# Revit family: STARC-REALWALL-PANEL
name_source: partatom
category: Specialty Equipment
revit_build: Autodesk Revit 2014 (Build: 20140709_2115(x64)
units: mm (PartAtom-declared; Revit-internal decimal feet)

## types (5) — shared parameters
ASTM Standard = E-84 CLASS A
Ceiling Height = 9' - 0"
Description = STARC SYSTEMS, INC REALWALL TEMPORARY CONTAINMENT SYSTEM PANEL
Height = 9' - 0"
ICRA Class = IV
Manufacturer = STARC SYSTEMS, INC.
URL = https://starcsystems.com

## per-type parameters (varying)
| type | Assembly Code | Type Comments | Width |
| S3-WM-24 |  | STARC SYSTEMS REALWALL 24 INCH TEMPORARY CONTAINMENT PANEL | 2' - 0" |
| S3-WM-32 |  | STARC SYSTEMS REALWALL 32 INCH TEMPORARY CONTAINMENT PANEL | 2' - 8" |
| S3-WM-12 | F1030900 | STARC SYSTEMS REALWALL 12 INCH TEMPORARY CONTAINMENT PANEL | 1' - 0" |
| S3-WM-18 |  | STARC SYSTEMS REALWALL 18 INCH TEMPORARY CONTAINMENT PANEL | 1' - 6" |
| S3-WM-42 |  | STARC SYSTEMS REALWALL 42 INCH TEMPORARY CONTAINMENT PANEL | 3' - 6" |

note: column(s) folded — value = type name in every type: Model

## geometry (parser evidence)
native form markers: Sweep x10
no freeform markers — native parametric forms only
